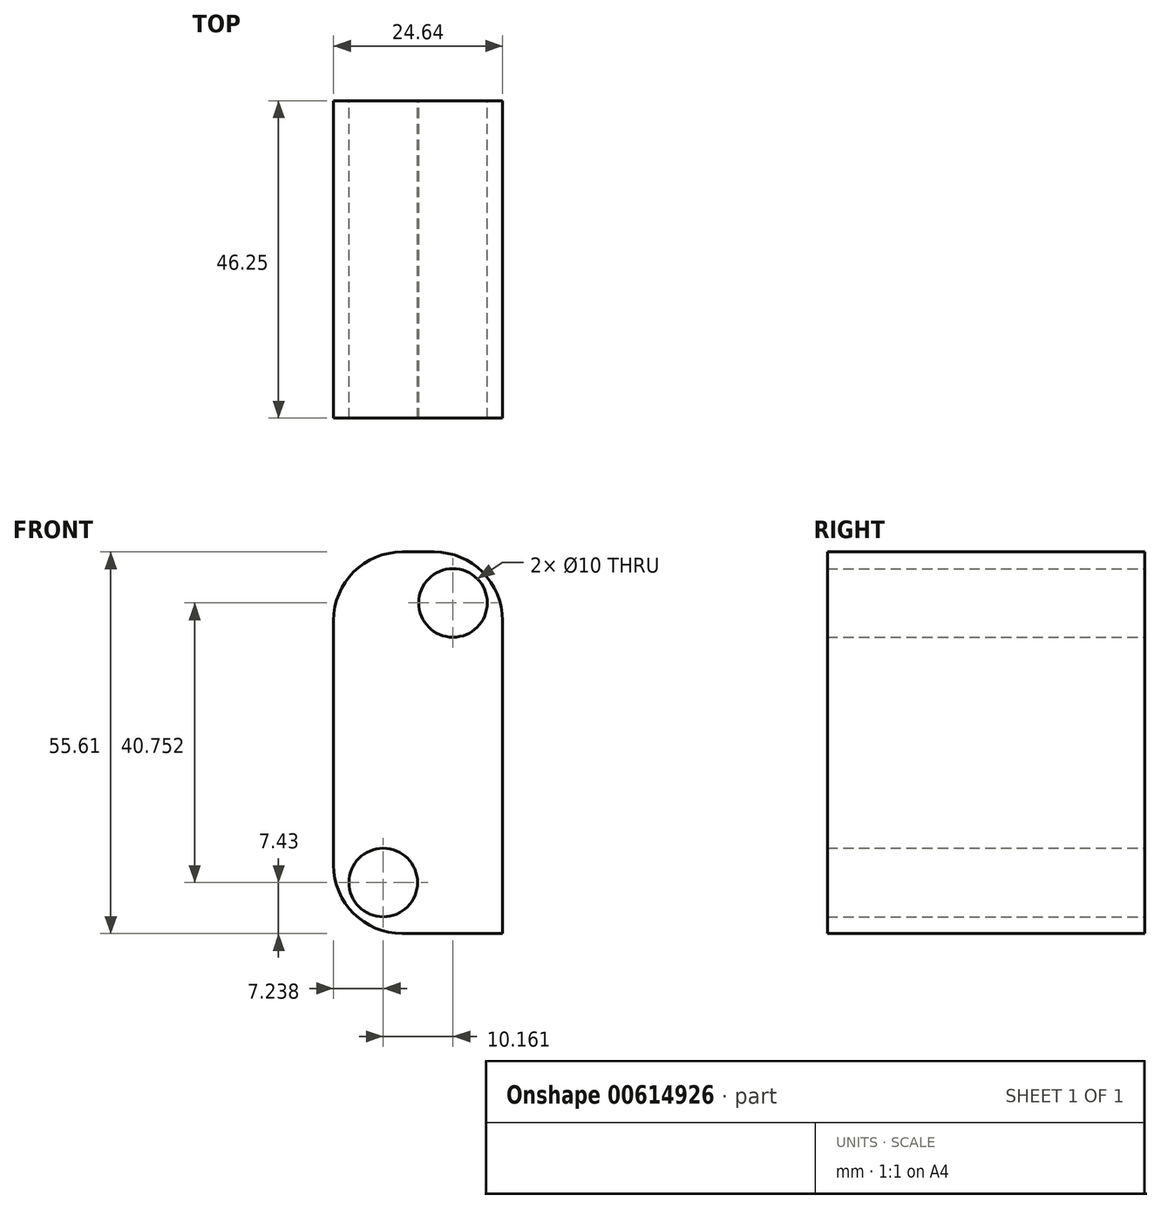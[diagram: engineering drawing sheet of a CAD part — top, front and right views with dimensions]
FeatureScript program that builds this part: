
annotation { "Feature Type Name" : "Feature", "Feature Type Description" : "" }
export const myFeature = defineFeature(function(context is Context, id is Id, definition is map)
    precondition{}
    {
        {
            var Q0;
            Q0=qCreatedBy(makeId("Front.planeOp"),FACE);
            var sketch = newSketch(context, id + "F0", { "sketchPlane" : qUnion([Q0])});
            skLineSegment(sketch, "E0", {"start": v(-6.2, -11.57) * mm, "end": v(23.8, -11.57) * mm});
            skCircle(sketch, "E1", {"center": v(23.8, -11.57) * mm, "radius": 5 * mm});
            skLineSegment(sketch, "E2", {"start": v(23.8, -11.57) * mm, "end": v(33.96, 29.18) * mm});
            skCircle(sketch, "E3", {"center": v(33.96, 29.18) * mm, "radius": 5 * mm});
            skLineSegment(sketch, "E4.bottom", {"start": v(31.2, 36.61) * mm, "end": v(26.56, 36.61) * mm});
            skLineSegment(sketch, "E4.top", {"start": v(41.2, -19) * mm, "end": v(26.56, -19) * mm});
            skLineSegment(sketch, "E4.left", {"start": v(41.2, 26.61) * mm, "end": v(41.2, -19) * mm});
            skLineSegment(sketch, "E4.right", {"start": v(16.56, 26.61) * mm, "end": v(16.56, -9) * mm});
            skPoint(sketch, "E4.middle", {"position": v(28.88, 8.8) * mm});
            skPoint(sketch, "E5.visualSharp", {"position": v(16.56, -19) * mm});
            skArc(sketch, "E5.filletArc", {"start": v(16.56, -9) * mm, "mid": v(19.49, -16.07) * mm, "end": v(26.56, -19) * mm});
            skPoint(sketch, "E6.visualSharp", {"position": v(16.56, 36.61) * mm});
            skArc(sketch, "E6.filletArc", {"start": v(26.56, 36.61) * mm, "mid": v(19.49, 33.68) * mm, "end": v(16.56, 26.61) * mm});
            skPoint(sketch, "E7.visualSharp", {"position": v(41.2, 36.61) * mm});
            skArc(sketch, "E7.filletArc", {"start": v(41.2, 26.61) * mm, "mid": v(38.27, 33.68) * mm, "end": v(31.2, 36.61) * mm});
            skLineSegment(sketch, "E8.left", {"start": v(41.2, -19) * mm, "end": v(41.2, 6) * mm});
            skLineSegment(sketch, "E9", {"start": v(41.2, 6) * mm, "end": v(41.2, 13) * mm});
            skLineSegment(sketch, "E10", {"start": v(41.2, 13) * mm, "end": v(41.2, 6) * mm});
            skSolve(sketch);
        }
        {
            var Q0;
            Q0=qSketchRegion(id+"F0",true);
            extrude(context, id + "F1", {"entities" : qUnion([Q0]), "depth" : 46.25 * mm, "offsetDistance" : 25 * mm});
        }
    });
